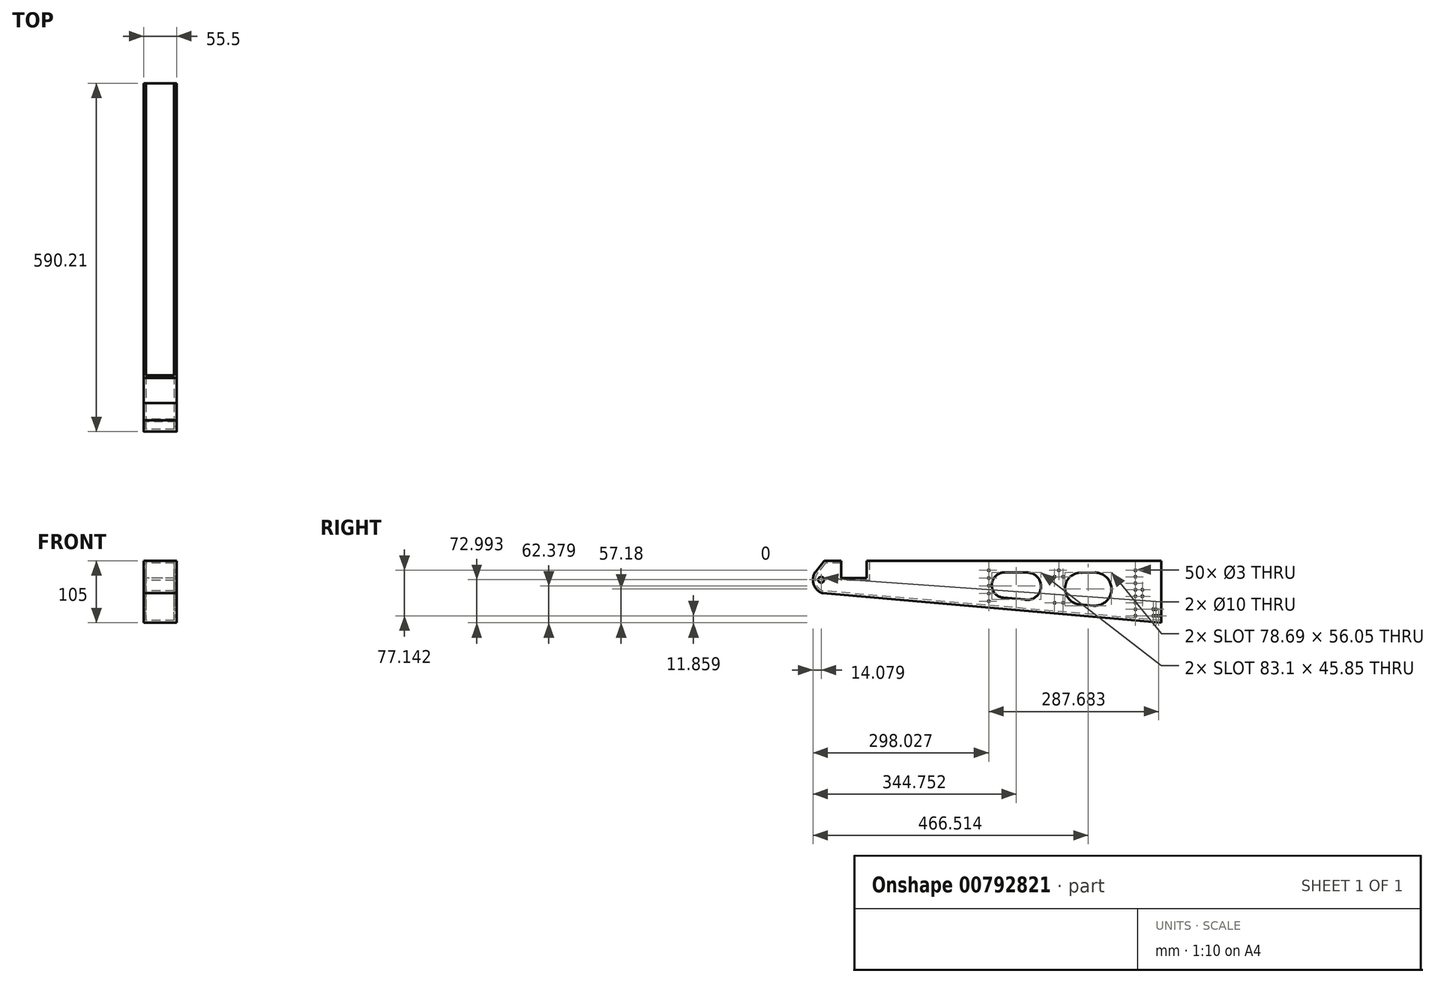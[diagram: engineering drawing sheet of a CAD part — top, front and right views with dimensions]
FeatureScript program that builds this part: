
annotation { "Feature Type Name" : "Feature", "Feature Type Description" : "" }
export const myFeature = defineFeature(function(context is Context, id is Id, definition is map)
    precondition{}
    {
        {
            var Q0;
            Q0=qCreatedBy(makeId("Right.planeOp"),FACE);
            var sketch = newSketch(context, id + "F0", { "sketchPlane" : qUnion([Q0])});
            skLineSegment(sketch, "E0", {"start": v(0, 49.9) * mm, "end": v(-499, 49.9) * mm});
            skLineSegment(sketch, "E1", {"start": v(0, 49.9) * mm, "end": v(0, -55.1) * mm});
            skLineSegment(sketch, "E2", {"start": v(-499, 49.9) * mm, "end": v(-499, 20.9) * mm});
            skLineSegment(sketch, "E3", {"start": v(-499, 20.9) * mm, "end": v(-542, 20.9) * mm});
            skLineSegment(sketch, "E4", {"start": v(-542, 20.9) * mm, "end": v(-542, 49.9) * mm});
            skLineSegment(sketch, "E5", {"start": v(-542, 49.9) * mm, "end": v(-571, 49.9) * mm});
            skLineSegment(sketch, "E6", {"start": v(0, -55.1) * mm, "end": v(-573.31, -4.94) * mm});
            skLineSegment(sketch, "E7", {"start": v(-571, 49.9) * mm, "end": v(-585.02, 32.42) * mm});
            skLineSegment(sketch, "E8", {"start": v(-84.4, 100.54) * mm, "end": v(-84.4, -78.64) * mm, "construction": true});
            skLineSegment(sketch, "E9", {"start": v(-162.9, 100.54) * mm, "end": v(-162.9, -78.64) * mm, "construction": true});
            skLineSegment(sketch, "E10", {"start": v(-204, 100.54) * mm, "end": v(-204, -78.64) * mm, "construction": true});
            skLineSegment(sketch, "E11", {"start": v(-287, 100.54) * mm, "end": v(-287, -78.64) * mm, "construction": true});
            skPoint(sketch, "E12.first.point", {"position": v(-204, 10.95) * mm});
            skPoint(sketch, "E13.third.point", {"position": v(-84.4, 0) * mm});
            skCircle(sketch, "E14", {"center": v(-112.42, 2.02) * mm, "radius": 28.09 * mm});
            skCircle(sketch, "E15", {"center": v(-136.15, 3.06) * mm, "radius": 26.93 * mm});
            skPoint(sketch, "E15.third.point", {"position": v(-162.9, 0) * mm});
            skCircle(sketch, "E16", {"center": v(-265.66, 8.87) * mm, "radius": 21.44 * mm});
            skPoint(sketch, "E16.third.point", {"position": v(-287, 10.95) * mm});
            skCircle(sketch, "E17", {"center": v(-226.85, 6.95) * mm, "radius": 23.05 * mm});
            skPoint(sketch, "E17.third.point", {"position": v(-204, 3.98) * mm});
            skLineSegment(sketch, "E18", {"start": v(-226.28, -16.1) * mm, "end": v(-267.52, -12.5) * mm});
            skLineSegment(sketch, "E19", {"start": v(-226.28, 29.98) * mm, "end": v(-267.52, 30.23) * mm});
            skLineSegment(sketch, "E20", {"start": v(-139.78, -23.62) * mm, "end": v(-115.05, -25.95) * mm});
            skLineSegment(sketch, "E21", {"start": v(-137.87, 29.93) * mm, "end": v(-112.61, 30.1) * mm});
            skArc(sketch, "E22", {"start": v(-585.02, 32.42) * mm, "mid": v(-589.13, 10.62) * mm, "end": v(-573.31, -4.94) * mm});
            skLineSegment(sketch, "E23", {"start": v(22.66, -55.1) * mm, "end": v(-476.63, -55.1) * mm, "construction": true});
            skSolve(sketch);
        }
        {
            var Q0;
            Q0 = qSketchRegion(id + "F0", true);
            extrude(context, id + "F1", {"entities" : qUnion([Q0]), "depth" : 55.5 * mm, "offsetDistance" : 25 * mm});
        }
        {
            var Q0;
            Q0=makeQuery(id+"F1.opExtrude","SWEPT_FACE",FACE,{"disambiguationData":[OSD([sQuery(id+"F0.wireOp",EDGE,"E1")])]});
            var Q1;
            Q1=makeQuery(id+"F1.opExtrude","SWEPT_FACE",FACE,{"disambiguationData":[OSD([sQuery(id+"F0.wireOp",EDGE,"E0")])]});
            var Q2;
            Q2=makeQuery(id+"F1.opExtrude","SWEPT_FACE",FACE,{"disambiguationData":[OSD([sQuery(id+"F0.wireOp",EDGE,"E4")])]});
            shell(context, id + "F2", {"entities" : qUnion([Q0, Q1, Q2]), "thickness" : 4 * mm});
        }
        {
            var Q0;
            Q0=makeQuery(id+"F1.opExtrude","CAP_FACE",FACE,{"disambiguationData":[OSD([sQuery(id+"F0.wireOp",EDGE,"E0"),sQuery(id+"F0.wireOp",EDGE,"E1"),sQuery(id+"F0.wireOp",EDGE,"E2"),sQuery(id+"F0.wireOp",EDGE,"E3"),sQuery(id+"F0.wireOp",EDGE,"E4"),sQuery(id+"F0.wireOp",EDGE,"E5"),sQuery(id+"F0.wireOp",EDGE,"E6"),sQuery(id+"F0.wireOp",EDGE,"E7"),sQuery(id+"F0.wireOp",EDGE,"i6E294zc-giSo-XzUo-B5Zy-jeYUpwJnYtjy"),sQuery(id+"F0.wireOp",EDGE,"E14"),sQuery(id+"F0.wireOp",EDGE,"E15"),sQuery(id+"F0.wireOp",EDGE,"E16"),sQuery(id+"F0.wireOp",EDGE,"E17"),sQuery(id+"F0.wireOp",EDGE,"E18"),sQuery(id+"F0.wireOp",EDGE,"E19"),sQuery(id+"F0.wireOp",EDGE,"E20"),sQuery(id+"F0.wireOp",EDGE,"E21")])],"isStart":false});
            var sketch = newSketch(context, id + "F3", { "sketchPlane" : qUnion([Q0])});
            skLineSegment(sketch, "E24", {"start": v(-43.75, 150.43) * mm, "end": v(-43.75, -143.83) * mm, "construction": true});
            skLineSegment(sketch, "E25", {"start": v(-199.09, 138.73) * mm, "end": v(-199.09, -122.78) * mm, "construction": true});
            skLineSegment(sketch, "E26", {"start": v(-505.54, 138.74) * mm, "end": v(-505.54, -113.44) * mm, "construction": true});
            skCircle(sketch, "E27", {"center": v(-43.75, 33.9) * mm, "radius": 1.5 * mm});
            skCircle(sketch, "E28", {"center": v(-43.75, 22.9) * mm, "radius": 1.5 * mm});
            skCircle(sketch, "E29", {"center": v(-43.75, 11.9) * mm, "radius": 1.5 * mm});
            skCircle(sketch, "E30", {"center": v(-43.75, 0.9) * mm, "radius": 1.5 * mm});
            skCircle(sketch, "E31", {"center": v(-43.75, -10.1) * mm, "radius": 1.5 * mm});
            skCircle(sketch, "E32", {"center": v(-43.75, -21.1) * mm, "radius": 1.5 * mm});
            skCircle(sketch, "E33", {"center": v(-43.75, -43.24) * mm, "radius": 1.5 * mm});
            skCircle(sketch, "E34", {"center": v(-43.75, -32.1) * mm, "radius": 1.5 * mm});
            skLineSegment(sketch, "E35", {"start": v(-60.69, -10.1) * mm, "end": v(22.1, -10.1) * mm, "construction": true});
            skLineSegment(sketch, "E36", {"start": v(-60.89, 0.9) * mm, "end": v(22.1, 0.9) * mm, "construction": true});
            skLineSegment(sketch, "E37", {"start": v(-32, 17.8) * mm, "end": v(-32, -20.8) * mm, "construction": true});
            skCircle(sketch, "E38", {"center": v(-32, 0.9) * mm, "radius": 1.5 * mm});
            skCircle(sketch, "E39", {"center": v(-32, -10.1) * mm, "radius": 1.5 * mm});
            skLineSegment(sketch, "E40", {"start": v(-34.86, -43.24) * mm, "end": v(14.5, -43.24) * mm, "construction": true});
            skLineSegment(sketch, "E41", {"start": v(-34.7, -32.1) * mm, "end": v(14.9, -32.1) * mm, "construction": true});
            skLineSegment(sketch, "E42", {"start": v(-4.5, 53.58) * mm, "end": v(-4.5, -57.98) * mm, "construction": true});
            skLineSegment(sketch, "E43", {"start": v(-9, 53.58) * mm, "end": v(-9, -57.98) * mm, "construction": true});
            skLineSegment(sketch, "E44", {"start": v(-13.5, -57.98) * mm, "end": v(-13.5, 53.58) * mm, "construction": true});
            skCircle(sketch, "E45", {"center": v(-4.5, -43.24) * mm, "radius": 1.5 * mm});
            skCircle(sketch, "E46", {"center": v(-9, -43.24) * mm, "radius": 1.5 * mm});
            skCircle(sketch, "E47", {"center": v(-9, -32.1) * mm, "radius": 1.5 * mm});
            skCircle(sketch, "E48", {"center": v(-13.5, -32.1) * mm, "radius": 1.5 * mm});
            skCircle(sketch, "E49", {"center": v(-13.5, -43.24) * mm, "radius": 1.5 * mm});
            skLineSegment(sketch, "E50", {"start": v(-166.25, 53.3) * mm, "end": v(-166.25, -52.2) * mm, "construction": true});
            skLineSegment(sketch, "E51", {"start": v(-173.5, 54.38) * mm, "end": v(-173.5, -52.47) * mm, "construction": true});
            skLineSegment(sketch, "E52", {"start": v(-180.75, -52.47) * mm, "end": v(-180.75, 54.93) * mm, "construction": true});
            skLineSegment(sketch, "E53", {"start": v(-43.75, 33.9) * mm, "end": v(-43.75, 32.4) * mm, "construction": true});
            skCircle(sketch, "E54", {"center": v(-166.25, -21.2) * mm, "radius": 1.5 * mm});
            skLineSegment(sketch, "E55", {"start": v(-187.95, 49.9) * mm, "end": v(26.3, 49.9) * mm, "construction": true});
            skLineSegment(sketch, "E56", {"start": v(22.22, 33.9) * mm, "end": v(-192.58, 33.9) * mm, "construction": true});
            skLineSegment(sketch, "E57", {"start": v(23.03, 22.9) * mm, "end": v(-192.58, 22.9) * mm, "construction": true});
            skLineSegment(sketch, "E58", {"start": v(25.49, -21.1) * mm, "end": v(-192.58, -21.21) * mm, "construction": true});
            skCircle(sketch, "E59", {"center": v(-180.75, 22.9) * mm, "radius": 1.5 * mm});
            skCircle(sketch, "E60", {"center": v(-180.75, -21.2) * mm, "radius": 1.5 * mm});
            skCircle(sketch, "E61", {"center": v(-166.25, 22.9) * mm, "radius": 1.5 * mm});
            skCircle(sketch, "E62", {"center": v(-173.5, 33.9) * mm, "radius": 1.5 * mm});
            skCircle(sketch, "E63", {"center": v(-292.18, 33.9) * mm, "radius": 1.5 * mm});
            skCircle(sketch, "E64", {"center": v(-292.18, -18.5) * mm, "radius": 1.5 * mm});
            skCircle(sketch, "E65", {"center": v(-292.18, 20.8) * mm, "radius": 1.5 * mm});
            skCircle(sketch, "E66", {"center": v(-292.18, 7.7) * mm, "radius": 1.5 * mm});
            skCircle(sketch, "E67", {"center": v(-292.18, -5.4) * mm, "radius": 1.5 * mm});
            skCircle(sketch, "E68", {"center": v(-576.13, 17.9) * mm, "radius": 5 * mm});
            skSolve(sketch);
        }
        {
            var Q0;
            Q0 = qSketchRegion(id + "F3", true);
            extrude(context, id + "F4", {"entities" : qUnion([Q0]), "operationType" : NewBodyOperationType.REMOVE, "oppositeDirection" : true, "depth" : 132 * mm, "offsetDistance" : 25 * mm});
        }
        {
            var Q0;
            Q0=makeQuery(id+"F1.opExtrude","CAP_FACE",FACE,{"disambiguationData":[OSD([sQuery(id+"F0.wireOp",EDGE,"E0"),sQuery(id+"F0.wireOp",EDGE,"E1"),sQuery(id+"F0.wireOp",EDGE,"E2"),sQuery(id+"F0.wireOp",EDGE,"E3"),sQuery(id+"F0.wireOp",EDGE,"E4"),sQuery(id+"F0.wireOp",EDGE,"E5"),sQuery(id+"F0.wireOp",EDGE,"E6"),sQuery(id+"F0.wireOp",EDGE,"E7"),sQuery(id+"F0.wireOp",EDGE,"i6E294zc-giSo-XzUo-B5Zy-jeYUpwJnYtjy"),sQuery(id+"F0.wireOp",EDGE,"E14"),sQuery(id+"F0.wireOp",EDGE,"E15"),sQuery(id+"F0.wireOp",EDGE,"E16"),sQuery(id+"F0.wireOp",EDGE,"E17"),sQuery(id+"F0.wireOp",EDGE,"E18"),sQuery(id+"F0.wireOp",EDGE,"E19"),sQuery(id+"F0.wireOp",EDGE,"E20"),sQuery(id+"F0.wireOp",EDGE,"E21")])],"isStart":false});
            var sketch = newSketch(context, id + "F5", { "sketchPlane" : qUnion([Q0])});
            skLineSegment(sketch, "E69", {"start": v(-298.9, 42.23) * mm, "end": v(-298.9, -20.62) * mm});
            skLineSegment(sketch, "E70", {"start": v(-298.9, -20.62) * mm, "end": v(-77.86, -39.9) * mm});
            skLineSegment(sketch, "E71", {"start": v(-77.86, -39.9) * mm, "end": v(-77.86, 42.23) * mm});
            skLineSegment(sketch, "E72", {"start": v(-77.86, 42.23) * mm, "end": v(-298.9, 42.23) * mm});
            skSolve(sketch);
        }
        {
            var Q0;
            Q0 = qSketchRegion(id + "F5", true);
            extrude(context, id + "F6", {"entities" : qUnion([Q0]), "operationType" : NewBodyOperationType.REMOVE, "oppositeDirection" : true, "depth" : 51.5 * mm, "offsetDistance" : 25 * mm, "hasSecondDirection" : true, "secondDirectionOppositeDirection" : true, "secondDirectionDepth" : 4 * mm});
        }
    });
